# Revit family: Frame_Grate_12_Inch_Z712-HGS
name_source: partatom
category: Plumbing Fixtures
units: mm (PartAtom-declared; Revit-internal decimal feet)

## family parameters
Always vertical = Yes
Cut with Voids When Loaded = No
Maintain Annotation Orientation = No
OmniClass Number = 23.70.50.21.24.14
OmniClass Title = Deck Waste Water Drains
Part Type = Normal
Room Calculation Point = No
Round Connector Dimension = Use Diameter
Shared = No
Work Plane-Based = No

## types (1)
- Z712-HDS
    Assembly Code = D2030300
    CW Connection = No
    CWFU = 0
    Default Elevation = 10 "
    Description = 12 [305] INCH WIDE REVEAL FRAME AND GRATE SYSTEM WITH GALVANIZED STEEL FRAME
    HW Connection = No
    HWFU = 0
    Manufacturer = Zurn Water, LLC
    Manufacurer Brand = Zurn
    Material_Grate = Steel - Zurn - Stainless - Type 304
    Model = Z712-HDG
    Modified Date = 11/25/2025
    Product Documentation Link = https://files.zurn.com
    Product Page URL = https://www.zurn.com
    Product data url = https://bimobject.com
    URL = www.zurn.com
    Vent Connection = No
    WFU = 1
    Waste Connection = Yes

## geometry (parser evidence)
native form markers: Blend x4, Sweep x3
no freeform markers — native parametric forms only
